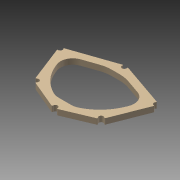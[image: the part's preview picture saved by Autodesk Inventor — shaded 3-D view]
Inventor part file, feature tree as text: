
AUTODESK INVENTOR PART (.ipt)
format: ipt  version: 2015 (Build 190159000, 159)  size: 175,616 bytes
history: native  units: mm
features: fillet x10, hole x4, extrude x2, sketch x2, mirror x1
ambient origin geometry x8: Origin, YZ Plane, XZ Plane, XY Plane, X Axis, Y Axis, Z Axis, Center Point
bodies: Solid4 (feature_tree)
feature tree (19):
  extrude  "Extrusion4"  Depth=264.2616mm
  hole  "Hole2"  [1 undecoded]
  hole  "Hole3"  [1 undecoded]
  hole  "Hole4"  [1 undecoded]
  hole  "Hole5"  [1 undecoded]
  fillet  "Fillet7"  Radius=27.432mm
  fillet  "Fillet8"  Radius=18.0mm
  fillet  "Fillet9"  Radius=10.0mm
  fillet  "Fillet10"  Radius=10.0mm
  fillet  "Fillet11"  Radius=1.5mm
  fillet  "Fillet12"  Radius=1.0mm
  extrude  "Extrusion5"  Depth=1.0mm
  fillet  "Fillet14"  Radius=2.0mm
  fillet  "Fillet15"  Radius=2.0mm
  fillet  "Fillet16"  Radius=2.0mm
  fillet  "Fillet17"  Radius=23.0mm
  mirror  "Mirror2"
  sketch  "Sketch1"  dims[d9=264.2616mm d11=161.8488mm]
  sketch  "Sketch5"  dims[d15=208.4832mm d20=109.1184mm d22=73.152mm d39=0.0mm d41=0.0mm d42=27.432mm d98=18.0mm d99=0.0mm d120=10.0mm d121=10.0mm d102=15.0mm d103=6.0mm d104=3.023mm d105=2.0mm d106=14.3117mm d107=8.0mm d108=20.594885mm d118=10.0mm d119=10.0mm d111=15.0mm d112=6.0mm d113=3.023mm d114=2.0mm d115=14.3117mm d116=8.0mm d117=20.594885mm d122=10.0mm d123=10.0mm d124=15.0mm d125=6.0mm d126=3.023mm d127=2.0mm d128=14.3117mm d129=8.0mm d130=20.594885mm d131=10.0mm d132=10.0mm d133=15.0mm d134=6.0mm d135=3.023mm d136=2.0mm d137=14.3117mm d138=8.0mm d139=20.594885mm d141=1.5mm d142=1.0mm d143=1.0mm d144=2.0mm d145=2.0mm d146=2.0mm d148=23.0mm d149=23.0mm d151=23.0mm d152=30.0mm d153=30.0mm d154=18.0mm d155=0.0mm d156=40.0mm d157=100.0mm d158=150.0mm d159=50.0mm]
note: 4 required parameter values undecoded (feature->parameter linkage not recoverable at this tier; creation-order binding heuristic only, values carry confidence <= 0.55)
